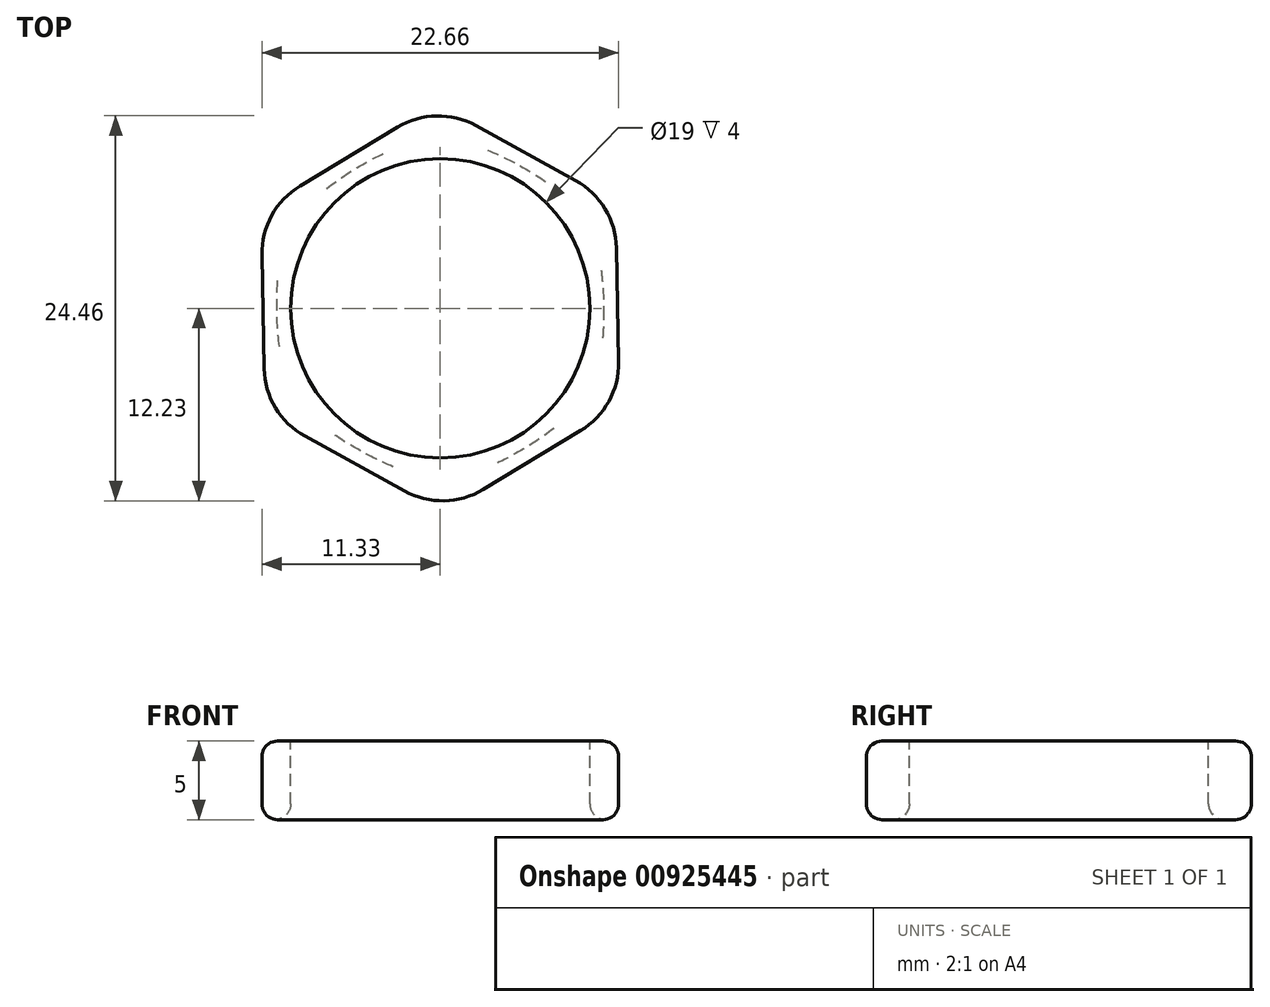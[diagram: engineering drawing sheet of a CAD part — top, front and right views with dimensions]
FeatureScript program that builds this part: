
annotation { "Feature Type Name" : "Feature", "Feature Type Description" : "" }
export const myFeature = defineFeature(function(context is Context, id is Id, definition is map)
    precondition{}
    {
        {
            var Q0;
            Q0=qCreatedBy(makeId("Top.planeOp"),FACE);
            var sketch = newSketch(context, id + "F0", { "sketchPlane" : qUnion([Q0])});
            skCircle(sketch, "E0", {"center": v(0, 0) * mm, "radius": 13 * mm});
            skCircle(sketch, "E1.cCircle", {"center": v(0, 0) * mm, "radius": 13 * mm, "construction": true});
            skLineSegment(sketch, "E1.0", {"start": v(11.38, -6.28) * mm, "end": v(0.25, -13) * mm});
            skLineSegment(sketch, "E1.1", {"start": v(0.25, -13) * mm, "end": v(-11.13, -6.72) * mm});
            skLineSegment(sketch, "E1.2", {"start": v(-11.13, -6.72) * mm, "end": v(-11.38, 6.28) * mm});
            skLineSegment(sketch, "E1.3", {"start": v(-11.38, 6.28) * mm, "end": v(-0.25, 13) * mm});
            skLineSegment(sketch, "E1.4", {"start": v(-0.25, 13) * mm, "end": v(11.13, 6.72) * mm});
            skLineSegment(sketch, "E1.5", {"start": v(11.13, 6.72) * mm, "end": v(11.38, -6.28) * mm});
            skSolve(sketch);
        }
        {
            var Q0;
            Q0=makeQuery(id+"F0.imprint","IMPRINT",FACE,{"disambiguationData":[TD([[makeQuery(id+"F0.imprint","IMPRINT",EDGE,{"derivedFrom":sQuery(id+"F0.wireOp",EDGE,"E1.0")}),-1.0]])]});
            extrude(context, id + "F1", {"entities" : qUnion([Q0]), "depth" : 5 * mm, "offsetDistance" : 25 * mm});
        }
        {
            var Q0;
            Q0=makeQuery(id+"F1.opExtrude","CAP_FACE",FACE,{"disambiguationData":[OSD([sQuery(id+"F0.wireOp",EDGE,"E1.0"),sQuery(id+"F0.wireOp",EDGE,"E1.1"),sQuery(id+"F0.wireOp",EDGE,"E1.2"),sQuery(id+"F0.wireOp",EDGE,"E1.3"),sQuery(id+"F0.wireOp",EDGE,"E1.4"),sQuery(id+"F0.wireOp",EDGE,"E1.5")])],"isStart":false});
            var sketch = newSketch(context, id + "F2", { "sketchPlane" : qUnion([Q0])});
            skCircle(sketch, "E2", {"center": v(0, 0) * mm, "radius": 9.5 * mm});
            skSolve(sketch);
        }
        {
            var Q0;
            Q0=makeQuery(id+"F2.imprint","IMPRINT",FACE,{"disambiguationData":[TD([[makeQuery(id+"F2.imprint","IMPRINT",EDGE,{"derivedFrom":sQuery(id+"F2.wireOp",EDGE,"E2")}),1.0]])]});
            extrude(context, id + "F3", {"entities" : qUnion([Q0]), "operationType" : NewBodyOperationType.REMOVE, "oppositeDirection" : true, "depth" : 25 * mm, "offsetDistance" : 25 * mm});
        }
        {
            var Q0;
            Q0=makeQuery(id+"F1.opExtrude","CAP_EDGE",EDGE,{"disambiguationData":[OSD([sQuery(id+"F0.wireOp",EDGE,"E1.5")])],"isStart":false});
            var Q1;
            Q1=makeQuery(id+"F1.opExtrude","CAP_EDGE",EDGE,{"disambiguationData":[OSD([sQuery(id+"F0.wireOp",EDGE,"E1.4")])],"isStart":false});
            var Q2;
            Q2=makeQuery(id+"F1.opExtrude","CAP_EDGE",EDGE,{"disambiguationData":[OSD([sQuery(id+"F0.wireOp",EDGE,"E1.3")])],"isStart":false});
            var Q3;
            Q3=makeQuery(id+"F1.opExtrude","CAP_EDGE",EDGE,{"disambiguationData":[OSD([sQuery(id+"F0.wireOp",EDGE,"E1.2")])],"isStart":false});
            var Q4;
            Q4=makeQuery(id+"F1.opExtrude","CAP_EDGE",EDGE,{"disambiguationData":[OSD([sQuery(id+"F0.wireOp",EDGE,"E1.1")])],"isStart":false});
            var Q5;
            Q5=makeQuery(id+"F1.opExtrude","CAP_EDGE",EDGE,{"disambiguationData":[OSD([sQuery(id+"F0.wireOp",EDGE,"E1.0")])],"isStart":false});
            var Q6;
            Q6=makeQuery(id+"F1.opExtrude","CAP_EDGE",EDGE,{"disambiguationData":[OSD([sQuery(id+"F0.wireOp",EDGE,"E1.0")])],"isStart":true});
            var Q7;
            Q7=makeQuery(id+"F1.opExtrude","CAP_EDGE",EDGE,{"disambiguationData":[OSD([sQuery(id+"F0.wireOp",EDGE,"E1.1")])],"isStart":true});
            var Q8;
            Q8=makeQuery(id+"F1.opExtrude","CAP_EDGE",EDGE,{"disambiguationData":[OSD([sQuery(id+"F0.wireOp",EDGE,"E1.5")])],"isStart":true});
            var Q9;
            Q9=makeQuery(id+"F1.opExtrude","CAP_EDGE",EDGE,{"disambiguationData":[OSD([sQuery(id+"F0.wireOp",EDGE,"E1.4")])],"isStart":true});
            var Q10;
            Q10=makeQuery(id+"F1.opExtrude","CAP_EDGE",EDGE,{"disambiguationData":[OSD([sQuery(id+"F0.wireOp",EDGE,"E1.2")])],"isStart":true});
            var Q11;
            Q11=makeQuery(id+"F1.opExtrude","CAP_EDGE",EDGE,{"disambiguationData":[OSD([sQuery(id+"F0.wireOp",EDGE,"E1.3")])],"isStart":true});
            var Q12;
            Q12=makeQuery(id+"F3.boolean.opBoolean","COPY",EDGE,{"derivedFrom":makeQuery(id+"F3.opExtrude","CAP_EDGE",EDGE,{"disambiguationData":[OSD([sQuery(id+"F2.wireOp",EDGE,"E2")])],"isStart":true})});
            var Q13;
            Q13=makeQuery(id+"F3.boolean.opBoolean","INTERSECT",EDGE,{"derivedFrom":[makeQuery(id+"F1.opExtrude","CAP_FACE",FACE,{"disambiguationData":[OSD([sQuery(id+"F0.wireOp",EDGE,"E1.0"),sQuery(id+"F0.wireOp",EDGE,"E1.1"),sQuery(id+"F0.wireOp",EDGE,"E1.2"),sQuery(id+"F0.wireOp",EDGE,"E1.3"),sQuery(id+"F0.wireOp",EDGE,"E1.4"),sQuery(id+"F0.wireOp",EDGE,"E1.5")])],"isStart":true}),makeQuery(id+"F3.opExtrude","SWEPT_FACE",FACE,{"disambiguationData":[OSD([sQuery(id+"F2.wireOp",EDGE,"E2")])]})]});
            fillet(context, id + "F4", {"entities" : qUnion([Q0, Q1, Q2, Q3, Q4, Q5, Q6, Q7, Q8, Q9, Q10, Q11, Q12, Q13]), "radius" : 1 * mm, "tangentPropagation" : true, "defaultsChanged" : true, "vertexSettings" : [], "allowEdgeOverflow" : false});
        }
        {
            var Q0;
            Q0=makeQuery(id+"F1.opExtrude","SWEPT_EDGE",EDGE,{"disambiguationData":[OSD([sQuery(id+"F0.wireOp",EDGE,"E0"),sQuery(id+"F0.wireOp",EDGE,"E1.3"),sQuery(id+"F0.wireOp",EDGE,"E1.4")])]});
            var Q1;
            Q1=makeQuery(id+"F1.opExtrude","SWEPT_EDGE",EDGE,{"disambiguationData":[OSD([sQuery(id+"F0.wireOp",EDGE,"E0"),sQuery(id+"F0.wireOp",EDGE,"E1.4"),sQuery(id+"F0.wireOp",EDGE,"E1.5")])]});
            var Q2;
            Q2=makeQuery(id+"F1.opExtrude","SWEPT_EDGE",EDGE,{"disambiguationData":[OSD([sQuery(id+"F0.wireOp",EDGE,"E0"),sQuery(id+"F0.wireOp",EDGE,"E1.2"),sQuery(id+"F0.wireOp",EDGE,"E1.3")])]});
            var Q3;
            Q3=makeQuery(id+"F1.opExtrude","SWEPT_EDGE",EDGE,{"disambiguationData":[OSD([sQuery(id+"F0.wireOp",EDGE,"E0"),sQuery(id+"F0.wireOp",EDGE,"E1.1"),sQuery(id+"F0.wireOp",EDGE,"E1.2")])]});
            var Q4;
            Q4=makeQuery(id+"F1.opExtrude","SWEPT_EDGE",EDGE,{"disambiguationData":[OSD([sQuery(id+"F0.wireOp",EDGE,"E0"),sQuery(id+"F0.wireOp",EDGE,"E1.0"),sQuery(id+"F0.wireOp",EDGE,"E1.1")])]});
            var Q5;
            Q5=makeQuery(id+"F1.opExtrude","SWEPT_EDGE",EDGE,{"disambiguationData":[OSD([sQuery(id+"F0.wireOp",EDGE,"E0"),sQuery(id+"F0.wireOp",EDGE,"E1.0"),sQuery(id+"F0.wireOp",EDGE,"E1.5")])]});
            fillet(context, id + "F5", {"entities" : qUnion([Q0, Q1, Q2, Q3, Q4, Q5]), "radius" : 5 * mm, "tangentPropagation" : true, "defaultsChanged" : true, "vertexSettings" : [], "allowEdgeOverflow" : false});
        }
    });
